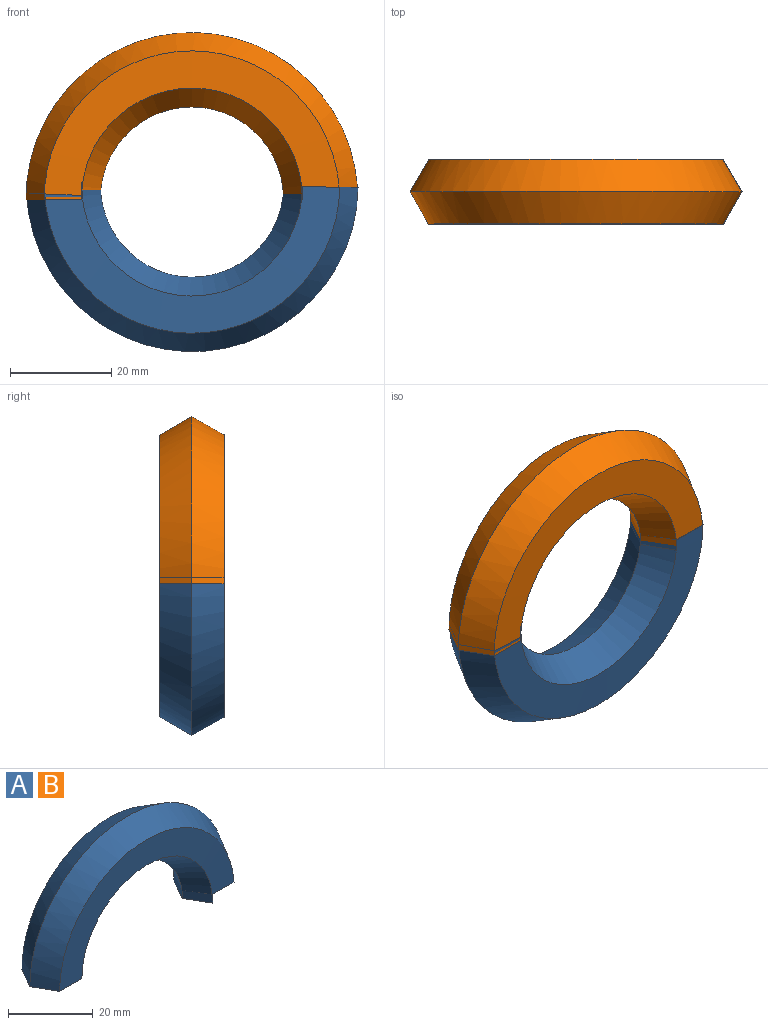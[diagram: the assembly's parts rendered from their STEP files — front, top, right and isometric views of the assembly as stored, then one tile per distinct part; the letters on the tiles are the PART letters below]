
ASSEMBLY  parts=2 mates=1
PART A: 10 faces, bbox 65.5x12.9x33.9 mm
  f0: bspline ~58.62x29.49mm, area 569mm2, adj f1,f3,f4,f7,f8
  f1: bspline ~65.39x32.97mm, area 697mm2, adj f0,f2,f3,f7
  f2: bspline ~65.39x32.97mm, area 698.3mm2, adj f1,f3,f5,f7
  f3: plane 14.66x12.77mm, normal (0,0,-1), area 89.4mm2, adj f0,f1,f2,f4,f5,f6
  f4: bspline ~43.35x21.83mm, area 461mm2, adj f0,f3,f6,f8
  f5: bspline ~58.85x30.36mm, area 571.6mm2, adj f2,f3,f6,f7,f9
  f6: bspline ~43.58x21.95mm, area 462.4mm2, adj f3,f4,f5,f9
  f7: plane 14.64x12.87mm, normal (-0.02,0,-1), area 87.5mm2, adj f0,f1,f2,f5,f8,f9
  f8: plane 6.47x3.74mm, normal (0.87,-0.49,-0.02), area 18.6mm2, adj f0,f4,f7,f9
  f9: plane 6.4x3.86mm, normal (0.86,0.51,-0.02), area 18.6mm2, adj f5,f6,f7,f8
PART B: same geometry as A
PLACE A rot(axis=(0,-1,0),178.9deg) t=(31.68,12.69,-0.28)mm
PLACE B t=(-19.16,12.69,-2.82)mm
MATE fastened A.f3 <-> B.f7  axis (0.02,0,1) through (31.68,12.69,-0.28)mm
